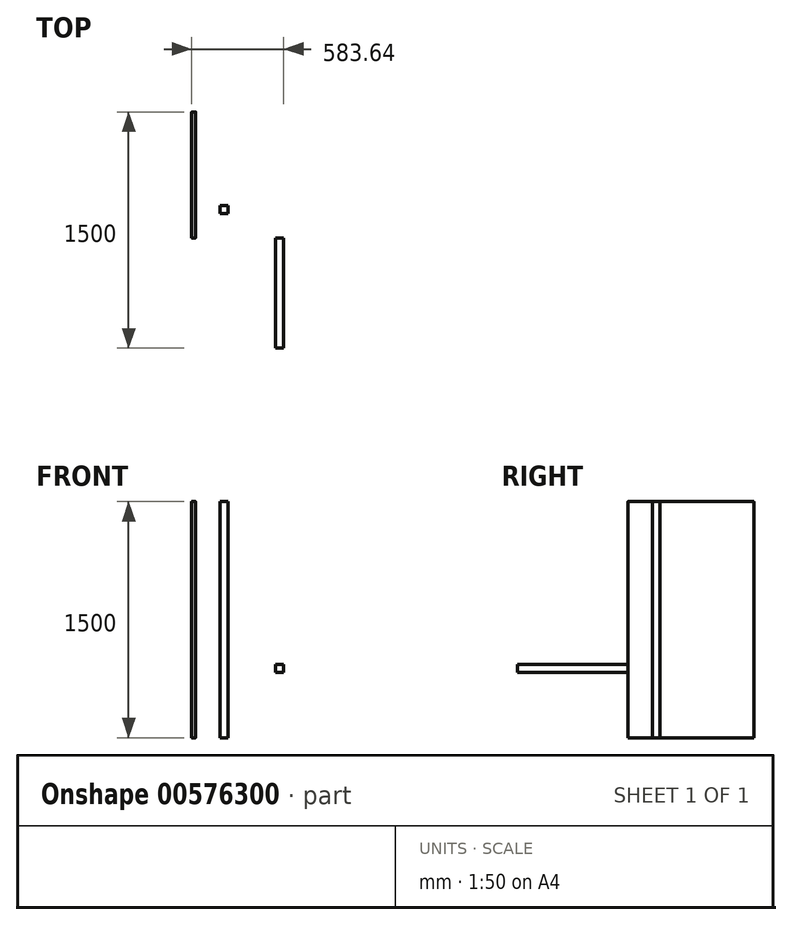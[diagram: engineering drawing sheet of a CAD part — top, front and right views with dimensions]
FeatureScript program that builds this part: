
annotation { "Feature Type Name" : "Feature", "Feature Type Description" : "" }
export const myFeature = defineFeature(function(context is Context, id is Id, definition is map)
    precondition{}
    {
        {
            var Q0;
            Q0=qCreatedBy(makeId("Right.planeOp"),FACE);
            var sketch = newSketch(context, id + "F0", { "sketchPlane" : qUnion([Q0])});
            skLineSegment(sketch, "E0.bottom", {"start": v(0, 0) * mm, "end": v(800, 0) * mm});
            skLineSegment(sketch, "E0.top", {"start": v(0, 1500) * mm, "end": v(800, 1500) * mm});
            skLineSegment(sketch, "E0.left", {"start": v(0, 0) * mm, "end": v(0, 1500) * mm});
            skLineSegment(sketch, "E0.right", {"start": v(800, 0) * mm, "end": v(800, 1500) * mm});
            skSolve(sketch);
        }
        {
            var Q0;
            Q0 = qSketchRegion(id + "F0", true);
            extrude(context, id + "F1", {"entities" : qUnion([Q0]), "depth" : 25 * mm, "offsetDistance" : 25 * mm});
        }
        {
            var Q0;
            Q0=makeQuery(id+"F1.opExtrude","CAP_EDGE",EDGE,{"disambiguationData":[OSD([sQuery(id+"F0.wireOp",EDGE,"E0.top")])],"isStart":false});
            var Q1;
            Q1=makeQuery(id+"F1.opExtrude","CAP_EDGE",EDGE,{"disambiguationData":[OSD([sQuery(id+"F0.wireOp",EDGE,"E0.left")])],"isStart":false});
            var Q2;
            Q2=makeQuery(id+"F1.opExtrude","CAP_EDGE",EDGE,{"disambiguationData":[OSD([sQuery(id+"F0.wireOp",EDGE,"E0.bottom")])],"isStart":false});
            var Q3;
            Q3=makeQuery(id+"F1.opExtrude","CAP_EDGE",EDGE,{"disambiguationData":[OSD([sQuery(id+"F0.wireOp",EDGE,"E0.right")])],"isStart":false});
            var Q4;
            Q4=makeQuery(id+"F1.opExtrude","CAP_EDGE",EDGE,{"disambiguationData":[OSD([sQuery(id+"F0.wireOp",EDGE,"E0.right")])],"isStart":true});
            var Q5;
            Q5=makeQuery(id+"F1.opExtrude","CAP_EDGE",EDGE,{"disambiguationData":[OSD([sQuery(id+"F0.wireOp",EDGE,"E0.bottom")])],"isStart":true});
            var Q6;
            Q6=makeQuery(id+"F1.opExtrude","CAP_EDGE",EDGE,{"disambiguationData":[OSD([sQuery(id+"F0.wireOp",EDGE,"E0.top")])],"isStart":true});
            var Q7;
            Q7=makeQuery(id+"F1.opExtrude","CAP_EDGE",EDGE,{"disambiguationData":[OSD([sQuery(id+"F0.wireOp",EDGE,"E0.left")])],"isStart":true});
            fillet(context, id + "F2", {"entities" : qUnion([Q0, Q1, Q2, Q3, Q4, Q5, Q6, Q7]), "radius" : .5 * mm, "tangentPropagation" : true, "allowEdgeOverflow" : false});
        }
        {
            var Q0;
            Q0=qCreatedBy(makeId("Top.planeOp"),FACE);
            var sketch = newSketch(context, id + "F3", { "sketchPlane" : qUnion([Q0])});
            skLineSegment(sketch, "E1.bottom", {"start": v(181.35, 204.22) * mm, "end": v(231.35, 204.22) * mm});
            skLineSegment(sketch, "E1.top", {"start": v(181.35, 154.22) * mm, "end": v(231.35, 154.22) * mm});
            skLineSegment(sketch, "E1.left", {"start": v(181.35, 204.22) * mm, "end": v(181.35, 154.22) * mm});
            skLineSegment(sketch, "E1.right", {"start": v(231.35, 204.22) * mm, "end": v(231.35, 154.22) * mm});
            skSolve(sketch);
        }
        {
            var Q0;
            Q0 = qSketchRegion(id + "F3", true);
            extrude(context, id + "F4", {"entities" : qUnion([Q0]), "depth" : 1500 * mm, "offsetDistance" : 25 * mm});
        }
        {
            var Q0;
            Q0=qCreatedBy(makeId("Front.planeOp"),FACE);
            var sketch = newSketch(context, id + "F5", { "sketchPlane" : qUnion([Q0])});
            skLineSegment(sketch, "E2.bottom", {"start": v(533.64, 464.58) * mm, "end": v(583.64, 464.58) * mm});
            skLineSegment(sketch, "E2.top", {"start": v(533.64, 414.58) * mm, "end": v(583.64, 414.58) * mm});
            skLineSegment(sketch, "E2.left", {"start": v(533.64, 464.58) * mm, "end": v(533.64, 414.58) * mm});
            skLineSegment(sketch, "E2.right", {"start": v(583.64, 464.58) * mm, "end": v(583.64, 414.58) * mm});
            skSolve(sketch);
        }
        {
            var Q0;
            Q0 = qSketchRegion(id + "F5", true);
            extrude(context, id + "F6", {"entities" : qUnion([Q0]), "depth" : 700 * mm, "offsetDistance" : 25 * mm});
        }
    });
